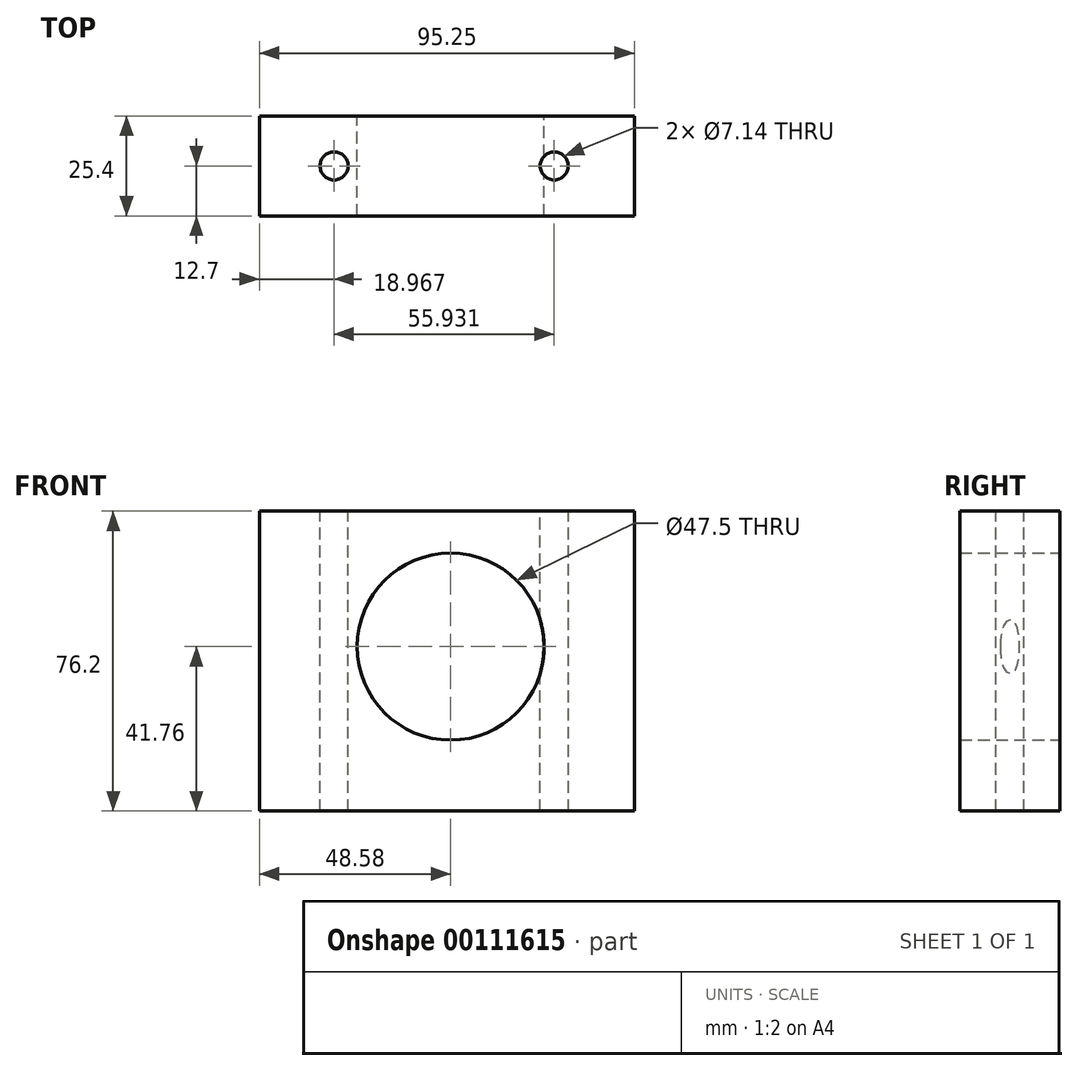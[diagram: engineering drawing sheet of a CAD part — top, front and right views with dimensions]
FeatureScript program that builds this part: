
annotation { "Feature Type Name" : "Feature", "Feature Type Description" : "" }
export const myFeature = defineFeature(function(context is Context, id is Id, definition is map)
    precondition{}
    {
        {
            var Q0;
            Q0=qCreatedBy(makeId("Front.planeOp"),FACE);
            var sketch = newSketch(context, id + "F0", { "sketchPlane" : qUnion([Q0])});
            skCircle(sketch, "E0", {"center": v(0, 0) * mm, "radius": 23.75 * mm});
            skLineSegment(sketch, "E1", {"start": v(-48.58, -41.76) * mm, "end": v(46.67, -41.76) * mm});
            skLineSegment(sketch, "E2", {"start": v(46.67, -41.76) * mm, "end": v(46.67, 34.44) * mm});
            skLineSegment(sketch, "E3", {"start": v(46.67, 34.44) * mm, "end": v(-48.58, 34.44) * mm});
            skLineSegment(sketch, "E4", {"start": v(-48.58, 34.44) * mm, "end": v(-48.58, -41.76) * mm});
            skSolve(sketch);
        }
        {
            var Q0;
            Q0=makeQuery(id+"F0.imprint","IMPRINT",FACE,{"disambiguationData":[TD([[makeQuery(id+"F0.imprint","IMPRINT",EDGE,{"derivedFrom":sQuery(id+"F0.wireOp",EDGE,"E0")}),-1.0]])]});
            extrude(context, id + "F1", {"entities" : qUnion([Q0]), "depth" : 25.4 * mm});
        }
        {
            var Q0;
            Q0=makeQuery(id+"F1.opExtrude","SWEPT_FACE",FACE,{"disambiguationData":[OSD([sQuery(id+"F0.wireOp",EDGE,"E3")])]});
            var sketch = newSketch(context, id + "F2", { "sketchPlane" : qUnion([Q0])});
            skCircle(sketch, "E5", {"center": v(-29.61, -12.7) * mm, "radius": 3.57 * mm});
            skCircle(sketch, "E6", {"center": v(26.32, -12.7) * mm, "radius": 3.57 * mm});
            skSolve(sketch);
        }
        {
            var Q0;
            Q0=sQuery(id+"F2.wireOp",VERTEX,"E5.center");
            var Q1;
            Q1=sQuery(id+"F2.wireOp",VERTEX,"E6.center");
            var Q2;
            Q2=makeQuery(id+"F1.opExtrude","SWEPT_BODY",BODY,{"disambiguationData":[OSD([sQuery(id+"F0.wireOp",EDGE,"E0"),sQuery(id+"F0.wireOp",EDGE,"E1"),sQuery(id+"F0.wireOp",EDGE,"E2"),sQuery(id+"F0.wireOp",EDGE,"E3"),sQuery(id+"F0.wireOp",EDGE,"E4")])]});
            hole(context, id + "F3", {"style" : HoleStyle.SIMPLE, "endStyle" : HoleEndStyle.THROUGH, "holeDiameter" : 7.14 * mm, "locations" : qUnion([Q0, Q1]), "scope" : qUnion([Q2]), "isTappedThrough" : true});
        }
    });
